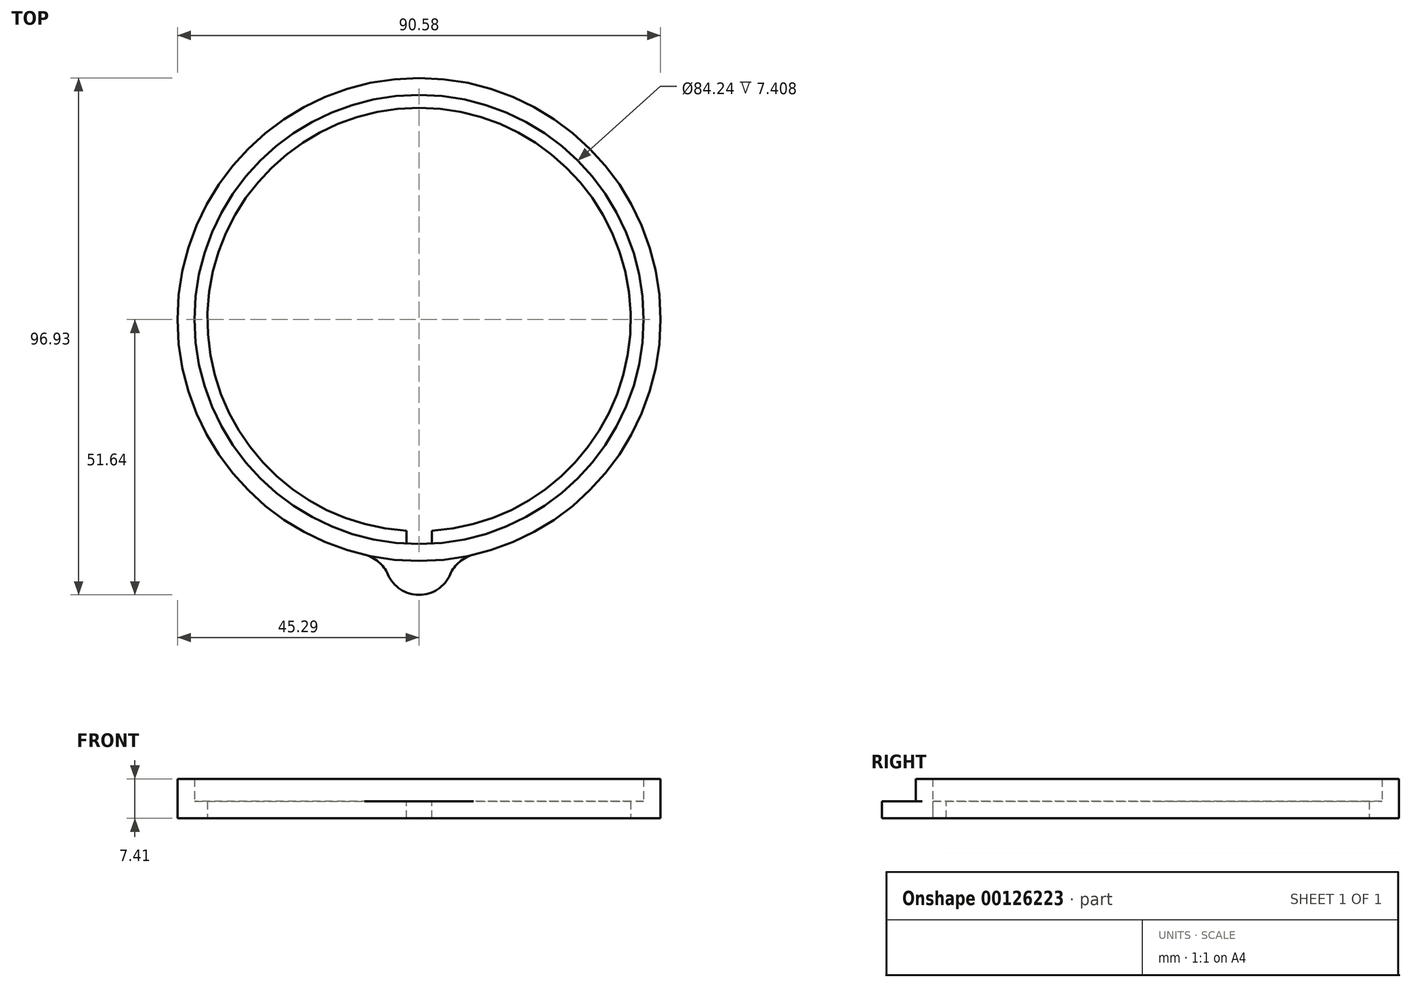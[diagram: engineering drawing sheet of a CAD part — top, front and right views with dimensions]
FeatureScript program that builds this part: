
annotation { "Feature Type Name" : "Feature", "Feature Type Description" : "" }
export const myFeature = defineFeature(function(context is Context, id is Id, definition is map)
    precondition{}
    {
        {
            var Q0;
            Q0=qCreatedBy(makeId("Front.planeOp"),FACE);
            var sketch = newSketch(context, id + "F0", { "sketchPlane" : qUnion([Q0])});
            skLineSegment(sketch, "E0", {"start": v(-42.12, 7.4) * mm, "end": v(-45.3, 7.4) * mm});
            skLineSegment(sketch, "E1", {"start": v(-45.3, 7.4) * mm, "end": v(-45.3, 0) * mm});
            skLineSegment(sketch, "E2", {"start": v(-45.3, 0) * mm, "end": v(-39.69, 0) * mm});
            skLineSegment(sketch, "E3", {"start": v(0, 0) * mm, "end": v(0, 7.4) * mm, "construction": true});
            skLineSegment(sketch, "E4", {"start": v(-42.12, 7.4) * mm, "end": v(-42.12, 3.17) * mm});
            skLineSegment(sketch, "E5", {"start": v(-42.12, 3.17) * mm, "end": v(-39.69, 3.18) * mm});
            skLineSegment(sketch, "E6", {"start": v(-39.69, 3.18) * mm, "end": v(-39.69, 0) * mm});
            skSolve(sketch);
        }
        {
            var Q0;
            Q0 = qSketchRegion(id + "F0", true);
            var Q1;
            Q1=sQuery(id+"F0.wireOp",EDGE,"E3");
            revolve(context, id + "F1", {"entities" : qUnion([Q0]), "axis" : qUnion([Q1]), "revolveType" : RevolveType.FULL});
        }
        {
            var Q0;
            Q0=makeQuery(id+"F1.opRevolve","SWEPT_FACE",FACE,{"disambiguationData":[OSD([sQuery(id+"F0.wireOp",EDGE,"E2")])]});
            var sketch = newSketch(context, id + "F2", { "sketchPlane" : qUnion([Q0])});
            skArc(sketch, "E7", {"start": v(5.83, 47.8) * mm, "mid": v(0, 51.64) * mm, "end": v(-5.83, 47.8) * mm});
            skCircle(sketch, "E8", {"center": v(0, 0) * mm, "radius": 45.3 * mm});
            skArc(sketch, "E9", {"start": v(-10.23, 44.12) * mm, "mid": v(-7.6, 45.44) * mm, "end": v(-5.83, 47.8) * mm});
            skArc(sketch, "E10", {"start": v(5.83, 47.8) * mm, "mid": v(7.6, 45.44) * mm, "end": v(10.23, 44.12) * mm});
            skSolve(sketch);
        }
        {
            var Q0;
            Q0=makeQuery(id+"F2.imprint","IMPRINT",FACE,{"disambiguationData":[TD([[makeQuery(id+"F2.imprint","IMPRINT",EDGE,{"derivedFrom":sQuery(id+"F2.wireOp",EDGE,"E7")}),1.0]])]});
            extrude(context, id + "F3", {"entities" : qUnion([Q0]), "operationType" : NewBodyOperationType.ADD, "oppositeDirection" : true, "depth" : 3.17 * mm});
        }
        {
            var Q0;
            Q0=makeQuery(id+"F1.opRevolve","SWEPT_FACE",FACE,{"disambiguationData":[OSD([sQuery(id+"F0.wireOp",EDGE,"E0")])]});
            var sketch = newSketch(context, id + "F4", { "sketchPlane" : qUnion([Q0])});
            skArc(sketch, "E11", {"start": v(-2.38, -42.05) * mm, "mid": v(0, -42.12) * mm, "end": v(2.38, -42.05) * mm});
            skArc(sketch, "E12", {"start": v(-2.38, -39.62) * mm, "mid": v(0, -39.69) * mm, "end": v(2.38, -39.62) * mm});
            skLineSegment(sketch, "E13", {"start": v(0, 0) * mm, "end": v(0, -42.12) * mm, "construction": true});
            skLineSegment(sketch, "E14", {"start": v(-2.38, -42.05) * mm, "end": v(-2.38, -39.62) * mm});
            skLineSegment(sketch, "E15", {"start": v(2.38, -39.62) * mm, "end": v(2.38, -42.05) * mm});
            skSolve(sketch);
        }
        {
            var Q0;
            Q0 = qSketchRegion(id + "F4", true);
            extrude(context, id + "F5", {"entities" : qUnion([Q0]), "operationType" : NewBodyOperationType.REMOVE, "endBound" : BoundingType.THROUGH_ALL, "oppositeDirection" : true, "depth" : 25.4 * mm});
        }
    });
